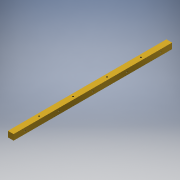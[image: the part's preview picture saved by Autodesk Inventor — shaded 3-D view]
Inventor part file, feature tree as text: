
AUTODESK INVENTOR PART (.ipt)
format: ipt  version: 2017 (Build 210142000, 142)  size: 126,976 bytes
history: native  units: in
note: dims shown in document units (in); Inventor stores cm internally (conversion verified against a paired STEP export)
features: sketch x3, hole x2, pattern_linear x2, extrude x1
ambient origin geometry x8: Origin, YZ Plane, XZ Plane, XY Plane, X Axis, Y Axis, Z Axis, Center Point
bodies: Solid1 (feature_tree)
feature tree (8):
  extrude  "Extrusion1"  Depth=0.25in
  hole  "Hole1"  [1 undecoded]
  pattern_linear  "Rectangular Pattern1"  Count1=5 Spacing1=1.5in
  pattern_linear  "Rectangular Pattern2"  Spacing1=0.75in  [1 undecoded]
  sketch  "Sketch1"  dims[d0=0.25in d2=0.25in]
  sketch  "Sketch2"  dims[d3=7.0in d4=0.0in d5=0.125in]
  sketch  "Sketch3"  dims[d6=0.5in d7=0.067in d8=0.75in d9=0.375in d10=0.25in d11=0.5635in d12=1.0in d13=0.8108in d21=1.9685in d23=1.5in d24=0.75in d27=0.8108in d28=0.5635in d29=0.25in d30=0.375in d31=1.0in d32=0.067in d33=1.25in d34=1.5748in d36=1.5in d37=0.125in]
  hole  "Hole2"  [1 undecoded]
note: 3 required parameter values undecoded (feature->parameter linkage not recoverable at this tier; creation-order binding heuristic only, values carry confidence <= 0.55)
